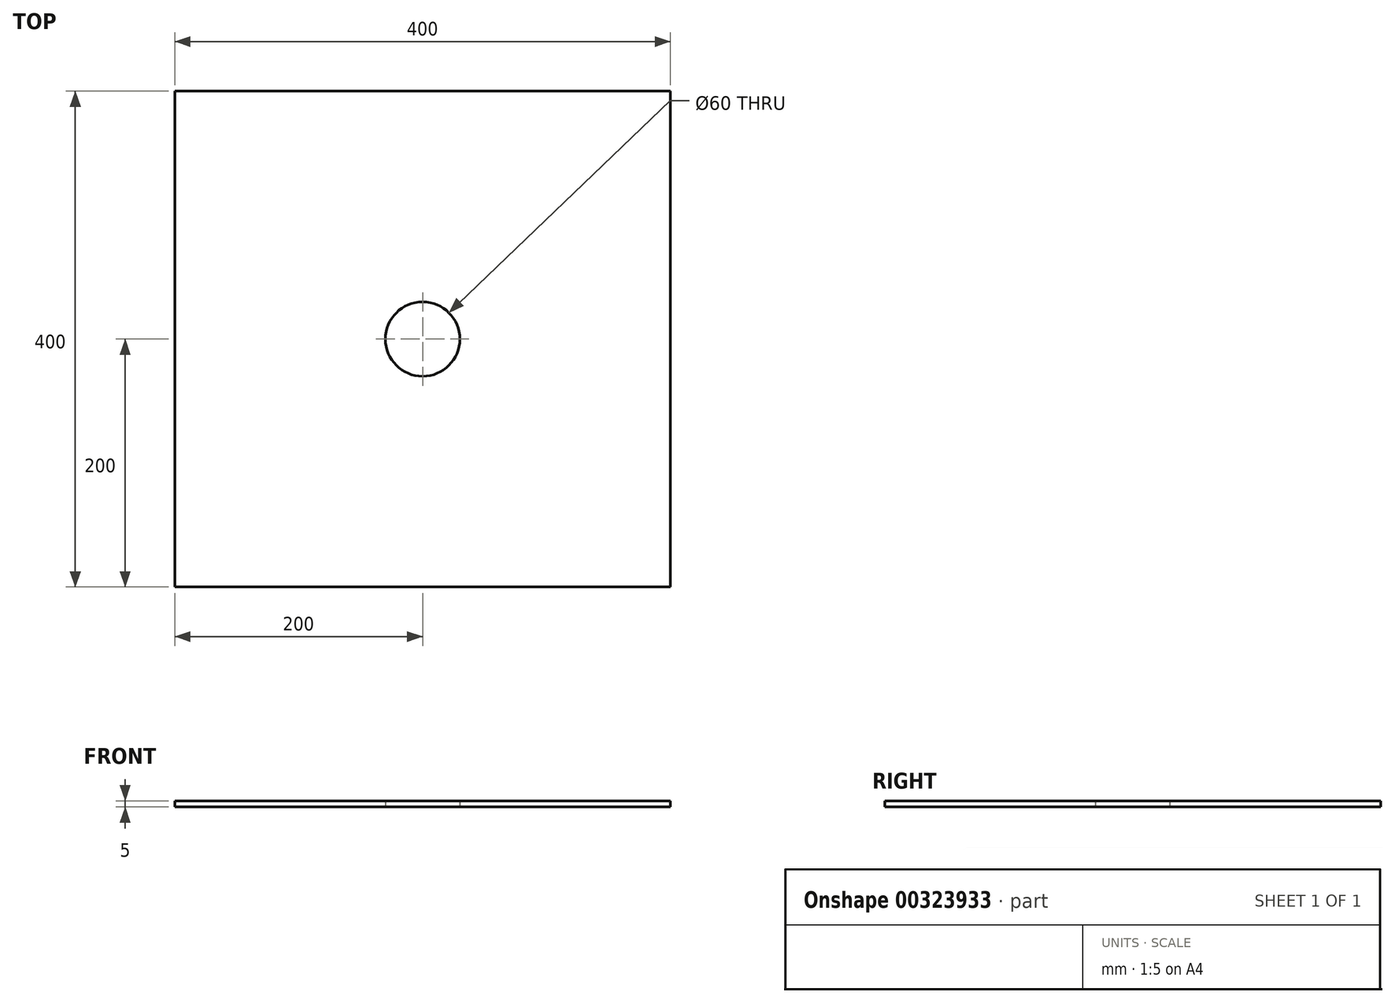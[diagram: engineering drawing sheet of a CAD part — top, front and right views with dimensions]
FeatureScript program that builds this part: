
annotation { "Feature Type Name" : "Feature", "Feature Type Description" : "" }
export const myFeature = defineFeature(function(context is Context, id is Id, definition is map)
    precondition{}
    {
        {
            var Q0;
            Q0=qCreatedBy(makeId("Top.planeOp"),FACE);
            var sketch = newSketch(context, id + "F0", { "sketchPlane" : qUnion([Q0])});
            skLineSegment(sketch, "E0.bottom", {"start": v(-200, 200) * mm, "end": v(200, 200) * mm});
            skLineSegment(sketch, "E0.top", {"start": v(-200, -200) * mm, "end": v(200, -200) * mm});
            skLineSegment(sketch, "E0.right", {"start": v(200, 200) * mm, "end": v(200, -200) * mm});
            skLineSegment(sketch, "E1", {"start": v(-200, 200) * mm, "end": v(-200, -200) * mm});
            skCircle(sketch, "E2", {"center": v(0, 0) * mm, "radius": 30 * mm});
            skSolve(sketch);
        }
        {
            var Q0;
            {var subQ3=sQuery(id+"F0.wireOp",EDGE,"E0.bottom");Q0=makeQuery(id+"F0.imprint","IMPRINT",FACE,{"disambiguationData":[TD([[makeQuery(id+"F0.imprint","IMPRINT",EDGE,{"derivedFrom":subQ3}),-1.0]])]});}
            extrude(context, id + "F1", {"entities" : qUnion([Q0]), "depth" : 5 * mm});
        }
    });
